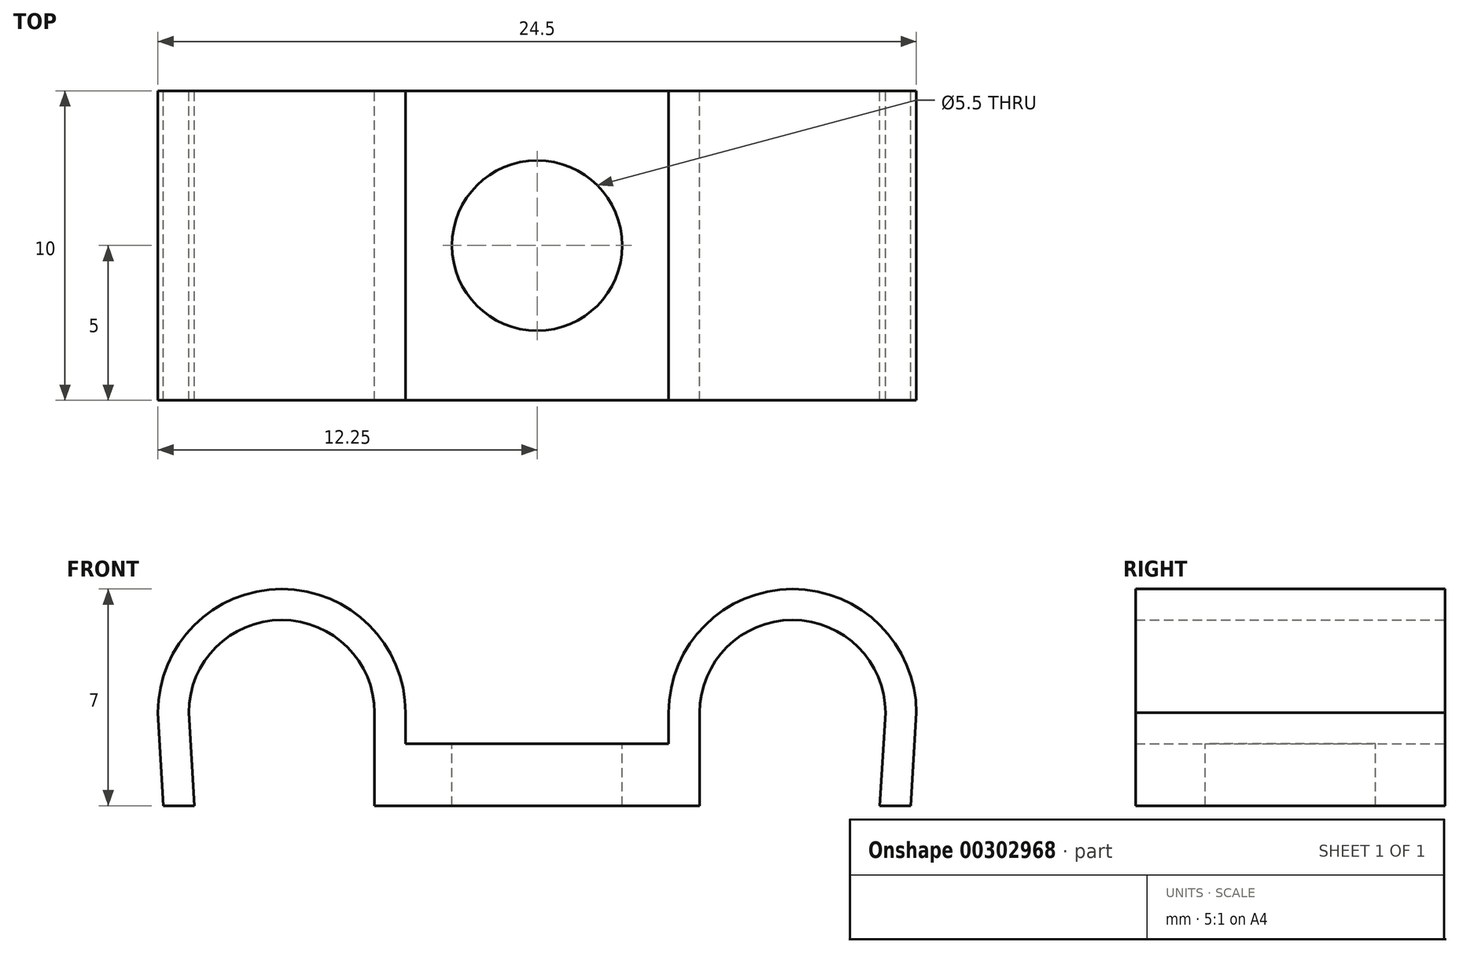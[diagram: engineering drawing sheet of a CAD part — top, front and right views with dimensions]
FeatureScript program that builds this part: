
annotation { "Feature Type Name" : "Feature", "Feature Type Description" : "" }
export const myFeature = defineFeature(function(context is Context, id is Id, definition is map)
    precondition{}
    {
        {
            var Q0;
            Q0=qCreatedBy(makeId("Front.planeOp"),FACE);
            var sketch = newSketch(context, id + "F0", { "sketchPlane" : qUnion([Q0])});
            skLineSegment(sketch, "E0", {"start": v(-16.46, 0) * mm, "end": v(18.26, 0) * mm, "construction": true});
            skLineSegment(sketch, "E1", {"start": v(0, 20.72) * mm, "end": v(0, -15.55) * mm, "construction": true});
            skLineSegment(sketch, "E2", {"start": v(-13.84, -3) * mm, "end": v(1, -3) * mm, "construction": true});
            skCircle(sketch, "E3", {"center": v(-8.25, 0) * mm, "radius": 4 * mm, "construction": true});
            skLineSegment(sketch, "E4.0", {"start": v(-13.84, -1) * mm, "end": v(1, -1) * mm, "construction": true});
            skLineSegment(sketch, "E5", {"start": v(-11.25, 0) * mm, "end": v(-11.02, -3.87) * mm, "construction": true});
            skLineSegment(sketch, "E6", {"start": v(-5.25, 0) * mm, "end": v(-5.25, -4.05) * mm, "construction": true});
            skArc(sketch, "E7", {"start": v(-12.25, 0) * mm, "mid": v(-8.25, 4) * mm, "end": v(-4.25, 0) * mm});
            skArc(sketch, "E8", {"start": v(-11.25, 0) * mm, "mid": v(-8.25, 3) * mm, "end": v(-5.25, 0) * mm});
            skLineSegment(sketch, "E9", {"start": v(-12.25, 0) * mm, "end": v(-12.25, 0) * mm});
            skLineSegment(sketch, "E10", {"start": v(-5.25, 0) * mm, "end": v(-5.25, -3) * mm});
            skLineSegment(sketch, "E11", {"start": v(-12.25, 0) * mm, "end": v(-12.07, -3) * mm});
            skLineSegment(sketch, "E12", {"start": v(-12.07, -3) * mm, "end": v(-11.07, -3) * mm});
            skLineSegment(sketch, "E13", {"start": v(-4.25, 0) * mm, "end": v(-4.25, -1) * mm});
            skLineSegment(sketch, "E14", {"start": v(-11.25, 0) * mm, "end": v(-11.07, -3) * mm});
            skArc(sketch, "E15", {"start": v(-5.25, 0) * mm, "mid": v(-8.25, 3) * mm, "end": v(-11.25, 0) * mm});
            skLineSegment(sketch, "E16", {"start": v(-1, 1.77) * mm, "end": v(-1, -4.41) * mm, "construction": true});
            skLineSegment(sketch, "E17.MirrorCS", {"start": v(12.25, 0) * mm, "end": v(12.07, -3) * mm});
            skLineSegment(sketch, "E18.MirrorCS", {"start": v(11.25, 0) * mm, "end": v(11.07, -3) * mm});
            skArc(sketch, "E19.MirrorCS", {"start": v(12.25, 0) * mm, "mid": v(8.25, 4) * mm, "end": v(4.25, 0) * mm});
            skArc(sketch, "E20.MirrorCS", {"start": v(5.25, 0) * mm, "mid": v(8.25, 3) * mm, "end": v(11.25, 0) * mm});
            skLineSegment(sketch, "E21.MirrorCS", {"start": v(5.25, 0) * mm, "end": v(5.25, -3) * mm});
            skLineSegment(sketch, "E22.MirrorCS", {"start": v(4.25, 0) * mm, "end": v(4.25, -1) * mm});
            skLineSegment(sketch, "E23.MirrorCS", {"start": v(12.07, -3) * mm, "end": v(11.07, -3) * mm});
            skLineSegment(sketch, "E24", {"start": v(-4.25, -1) * mm, "end": v(4.25, -1) * mm});
            skLineSegment(sketch, "E25", {"start": v(-5.25, -3) * mm, "end": v(5.25, -3) * mm});
            skSolve(sketch);
        }
        {
            var Q0;
            Q0 = qSketchRegion(id + "F0", true);
            extrude(context, id + "F1", {"entities" : qUnion([Q0]), "depth" : 10 * mm});
        }
        {
            var Q0;
            Q0=makeQuery(id+"F1.opExtrude","SWEPT_FACE",FACE,{"disambiguationData":[OSD([sQuery(id+"F0.wireOp",EDGE,"E24")])]});
            var sketch = newSketch(context, id + "F2", { "sketchPlane" : qUnion([Q0])});
            skCircle(sketch, "E26", {"center": v(0, -5) * mm, "radius": 2.75 * mm});
            skSolve(sketch);
        }
        {
            var Q0;
            Q0=makeQuery(id+"F2.imprint","IMPRINT",FACE,{"disambiguationData":[TD([[makeQuery(id+"F2.imprint","IMPRINT",EDGE,{"derivedFrom":sQuery(id+"F2.wireOp",EDGE,"E26")}),1.0]])]});
            extrude(context, id + "F3", {"entities" : qUnion([Q0]), "operationType" : NewBodyOperationType.REMOVE, "oppositeDirection" : true, "depth" : 2.5 * mm});
        }
    });
